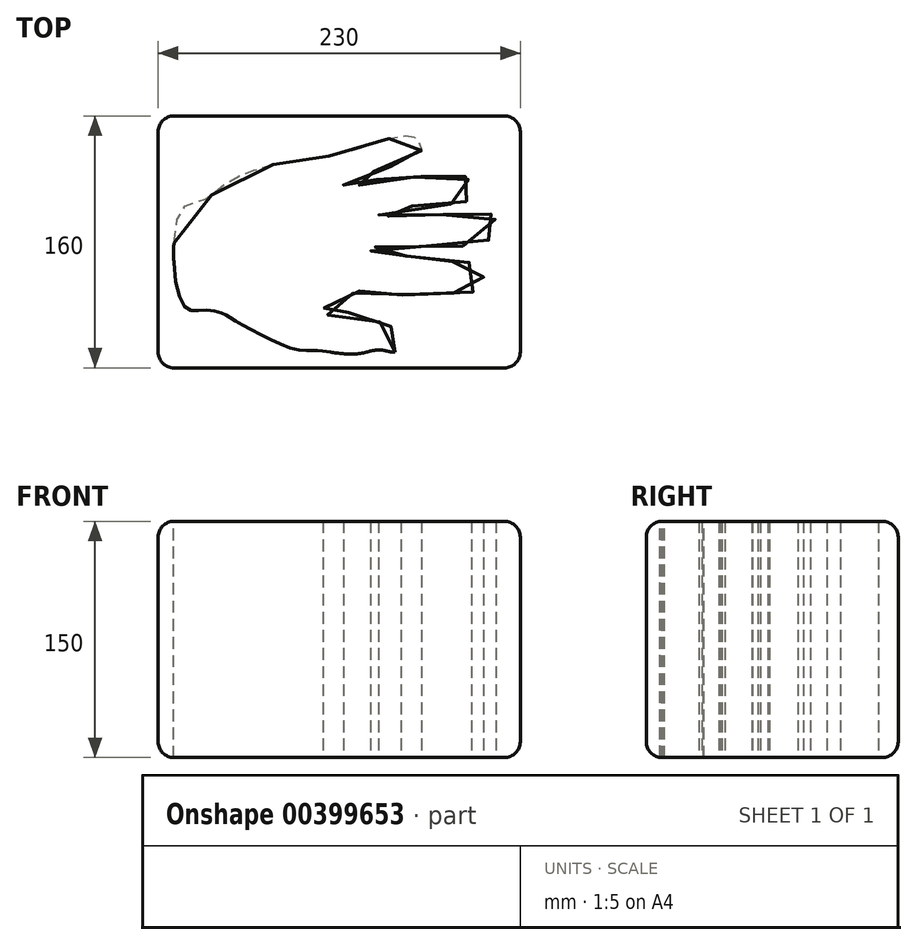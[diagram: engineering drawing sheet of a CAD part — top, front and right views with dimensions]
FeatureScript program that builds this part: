
annotation { "Feature Type Name" : "Feature", "Feature Type Description" : "" }
export const myFeature = defineFeature(function(context is Context, id is Id, definition is map)
    precondition{}
    {
        {
            var Q0;
            Q0=qCreatedBy(makeId("Top.planeOp"),FACE);
            var sketch = newSketch(context, id + "F0", { "sketchPlane" : qUnion([Q0])});
            skLineSegment(sketch, "E0.bottom", {"start": v(-115, 80) * mm, "end": v(115, 80) * mm});
            skLineSegment(sketch, "E0.top", {"start": v(-115, -80) * mm, "end": v(115, -80) * mm});
            skLineSegment(sketch, "E0.left", {"start": v(-115, 80) * mm, "end": v(-115, -80) * mm});
            skLineSegment(sketch, "E0.right", {"start": v(115, 80) * mm, "end": v(115, -80) * mm});
            skPoint(sketch, "E0.middle", {"position": v(0, 0) * mm});
            skSolve(sketch);
        }
        {
            var Q0;
            Q0 = qSketchRegion(id + "F0", true);
            extrude(context, id + "F1", {"entities" : qUnion([Q0]), "depth" : 150 * mm});
        }
        {
            var Q0;
            Q0=makeQuery(id+"F1.opExtrude","SWEPT_FACE",FACE,{"disambiguationData":[OSD([sQuery(id+"F0.wireOp",EDGE,"E0.top")])]});
            var Q1;
            Q1=makeQuery(id+"F1.opExtrude","SWEPT_FACE",FACE,{"disambiguationData":[OSD([sQuery(id+"F0.wireOp",EDGE,"E0.bottom")])]});
            var Q2;
            Q2=makeQuery(id+"F1.opExtrude","SWEPT_FACE",FACE,{"disambiguationData":[OSD([sQuery(id+"F0.wireOp",EDGE,"E0.right")])]});
            var Q3;
            Q3=makeQuery(id+"F1.opExtrude","SWEPT_FACE",FACE,{"disambiguationData":[OSD([sQuery(id+"F0.wireOp",EDGE,"E0.left")])]});
            fillet(context, id + "F2", {"entities" : qUnion([Q0, Q1, Q2, Q3]), "radius" : 10 * mm, "tangentPropagation" : true, "allowEdgeOverflow" : false});
        }
        {
            var Q0;
            Q0=makeQuery(id+"F1.opExtrude","CAP_FACE",FACE,{"disambiguationData":[OSD([sQuery(id+"F0.wireOp",EDGE,"E0.bottom"),sQuery(id+"F0.wireOp",EDGE,"E0.top"),sQuery(id+"F0.wireOp",EDGE,"E0.left"),sQuery(id+"F0.wireOp",EDGE,"E0.right")])],"isStart":false});
            var sketch = newSketch(context, id + "F3", { "sketchPlane" : qUnion([Q0])});
            skFitSpline(sketch, "E1", {"points": [v(-86.86, 26.38) * mm, v(-71.87, 37.37) * mm, v(-43.88, 48.62) * mm, v(-24.38, 52.37) * mm, v(-7.64, 54.37) * mm, v(19.6, 61.62) * mm, v(33.1, 65.86) * mm, v(46.34, 67.11) * mm, v(50.84, 63.11) * mm, v(51.84, 56.37) * mm, v(44.1, 51.37) * mm, v(20.85, 44.37) * mm, v(2.6, 36.12) * mm, v(5.6, 34.62) * mm, v(21.1, 38.87) * mm, v(34.35, 41.12) * mm, v(59.1, 41.87) * mm, v(77.58, 42.87) * mm, v(83.08, 37.62) * mm, v(83.58, 29.88) * mm, v(79.58, 25.13) * mm, v(55.1, 23.88) * mm, v(25.1, 17.38) * mm, v(37.85, 16.38) * mm, v(65.59, 17.38) * mm, v(91.33, 19.63) * mm, v(98.83, 14.88) * mm, v(98.83, 6.38) * mm, v(92.83, 0) * mm, v(52.84, -2.36) * mm, v(20.85, -4.36) * mm, v(20.85, -8.61) * mm, v(34.35, -7.61) * mm, v(53.1, -12.11) * mm, v(78.08, -12.61) * mm, v(90.33, -17.11) * mm, v(90.83, -26.86) * mm, v(83.83, -32.1) * mm, v(54.34, -32.1) * mm, v(37.85, -33.6) * mm, v(18.85, -30.1) * mm, v(4.86, -34.1) * mm, v(-8.64, -40.6) * mm, v(-9.89, -46.1) * mm, v(0, -44.6) * mm, v(14.85, -47.6) * mm, v(33.1, -53.85) * mm, v(39.1, -61.35) * mm, v(36.85, -69.6) * mm, v(26.1, -68.6) * mm, v(11.36, -71.1) * mm, v(-10.39, -69.34) * mm, v(-16.14, -69.1) * mm, v(-28.13, -68.1) * mm, v(-53.37, -57.1) * mm, v(-68.62, -48.6) * mm, v(-73.62, -45.6) * mm, v(-86.61, -43.35) * mm, v(-99.11, -40.1) * mm, v(-100.6, 19.88) * mm, v(-86.86, 26.38) * mm]});
            skSolve(sketch);
        }
        {
            var Q0;
            Q0 = qSketchRegion(id + "F3", true);
            extrude(context, id + "F4", {"entities" : qUnion([Q0]), "operationType" : NewBodyOperationType.REMOVE, "oppositeDirection" : true, "depth" : 170 * mm});
        }
    });
